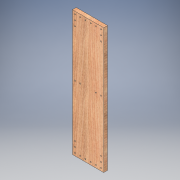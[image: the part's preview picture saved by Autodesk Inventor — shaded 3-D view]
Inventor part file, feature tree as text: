
AUTODESK INVENTOR PART (.ipt)
format: ipt  version: 2018 (Build 220112000, 112)  size: 187,392 bytes
history: native  units: in
note: dims shown in document units (in); Inventor stores cm internally (conversion verified against a paired STEP export)
features: extrude x4, sketch x4
ambient origin geometry x8: Origin, YZ Plane, XZ Plane, XY Plane, X Axis, Y Axis, Z Axis, Center Point
bodies: Solid1 (feature_tree)
feature tree (8):
  extrude  "Extrusion1"  Depth=24.0in
  extrude  "Extrusion2"  Depth=0.75in
  extrude  "Extrusion3"  Depth=0.2031in
  extrude  "Extrusion4"  Depth=0.75in
  sketch  "Sketch1"  dims[d0=6.0in d1=24.0in]
  sketch  "Sketch2"  dims[d2=0.75in d3=0.0in d4=0.5in]
  sketch  "Sketch3"  dims[d5=0.5in d6=0.2031in]
  sketch  "Sketch4"  dims[d7=0.75in d8=0.0in d9=1.0in d10=1.0in d11=1.0in d12=1.0in d13=0.75in d14=0.0in d15=11.5in d17=0.5in d18=1.0in d19=0.2031in d20=0.75in d21=0.0in]
